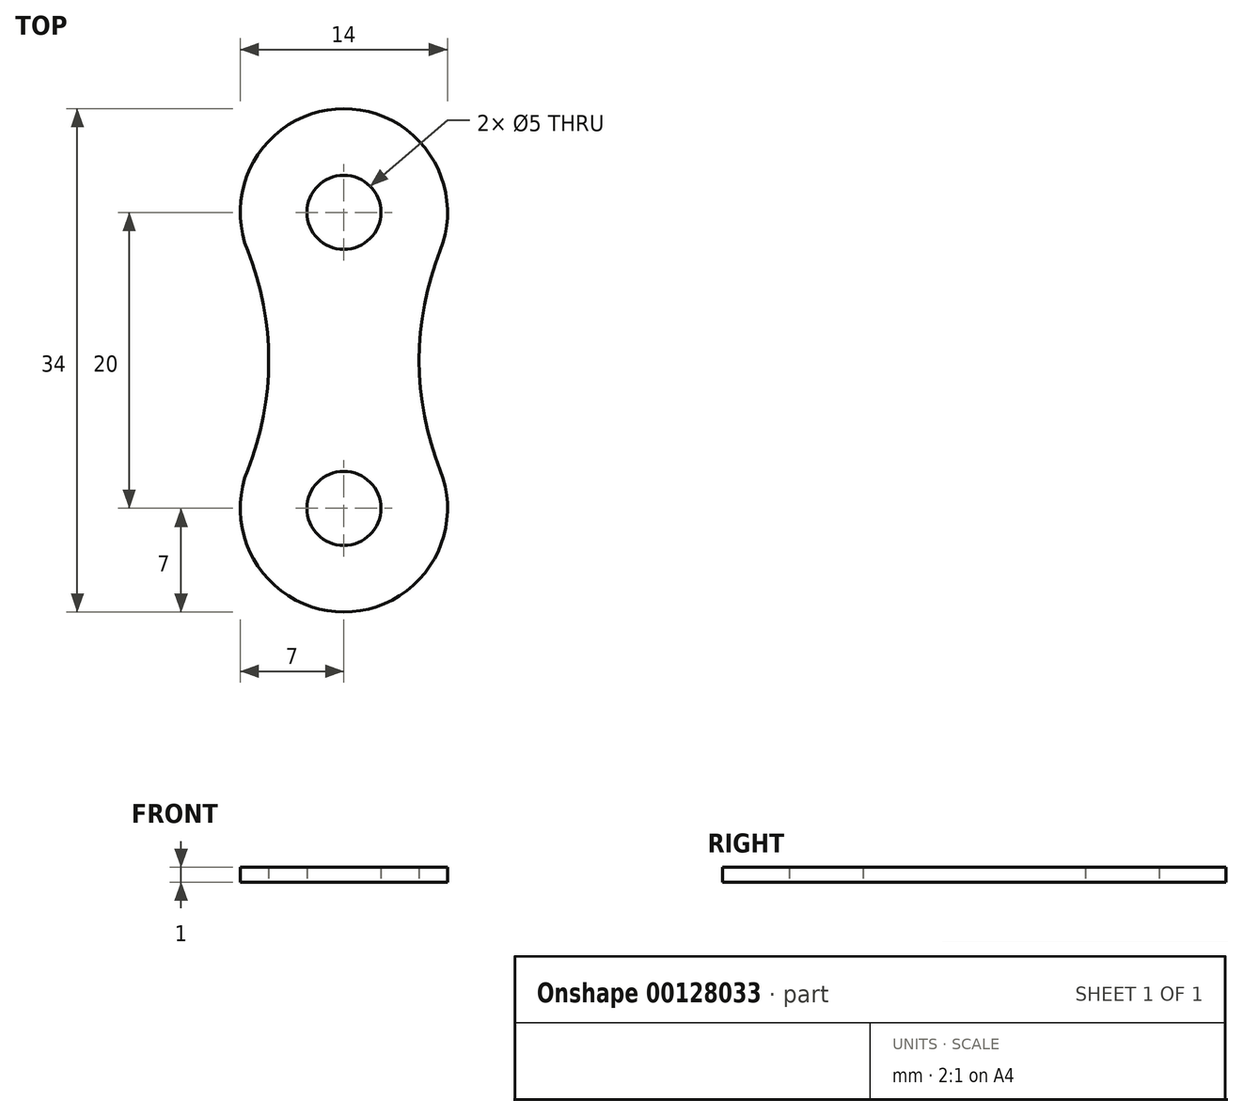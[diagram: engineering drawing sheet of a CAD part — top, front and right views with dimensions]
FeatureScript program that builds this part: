
annotation { "Feature Type Name" : "Feature", "Feature Type Description" : "" }
export const myFeature = defineFeature(function(context is Context, id is Id, definition is map)
    precondition{}
    {
        {
            var Q0;
            Q0=qCreatedBy(makeId("Top.planeOp"),FACE);
            var sketch = newSketch(context, id + "F0", { "sketchPlane" : qUnion([Q0])});
            skArc(sketch, "E0", {"start": v(6.5, 7.4) * mm, "mid": v(0, 17) * mm, "end": v(-6.5, 7.4) * mm});
            skArc(sketch, "E1", {"start": v(-6.5, -7.4) * mm, "mid": v(0, -17) * mm, "end": v(6.5, -7.4) * mm});
            skArc(sketch, "E2", {"start": v(-6.5, -7.4) * mm, "mid": v(-5.08, 0) * mm, "end": v(-6.5, 7.4) * mm});
            skArc(sketch, "E3", {"start": v(6.5, 7.4) * mm, "mid": v(5.08, 0) * mm, "end": v(6.5, -7.4) * mm});
            skCircle(sketch, "E4", {"center": v(0, 10) * mm, "radius": 2.5 * mm});
            skCircle(sketch, "E5", {"center": v(0, -10) * mm, "radius": 2.5 * mm});
            skSolve(sketch);
        }
        {
            var Q0;
            Q0=makeQuery(id+"F0.imprint","IMPRINT",FACE,{"disambiguationData":[TD([[makeQuery(id+"F0.imprint","IMPRINT",EDGE,{"derivedFrom":sQuery(id+"F0.wireOp",EDGE,"E0")}),1.0]])]});
            extrude(context, id + "F1", {"entities" : qUnion([Q0]), "depth" : 1 * mm});
        }
    });
